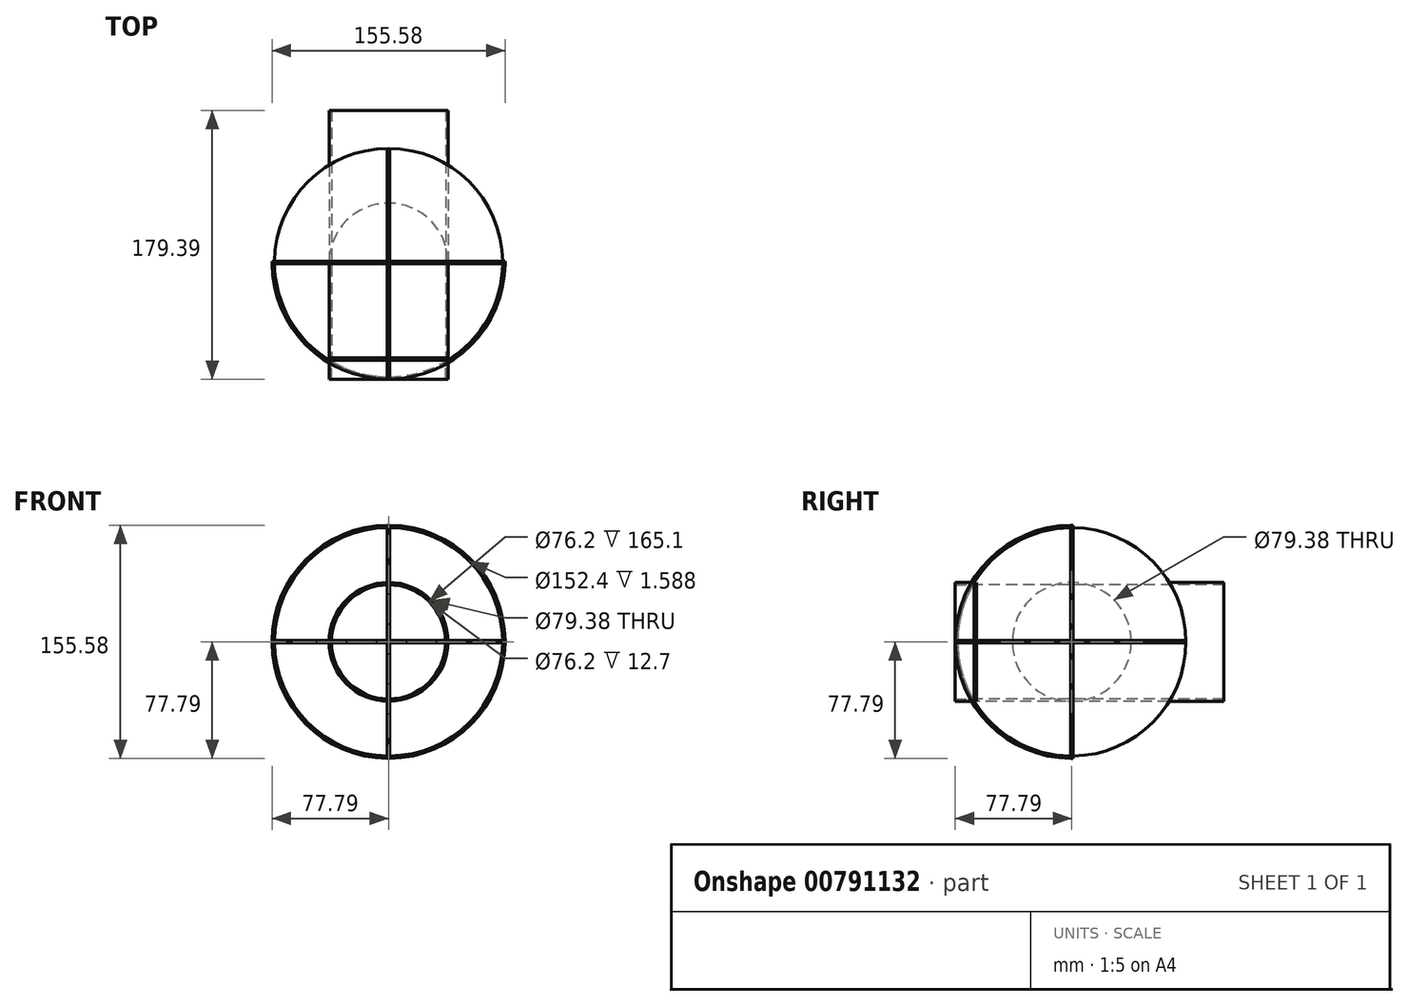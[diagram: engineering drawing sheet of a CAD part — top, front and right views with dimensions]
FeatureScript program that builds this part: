
annotation { "Feature Type Name" : "Feature", "Feature Type Description" : "" }
export const myFeature = defineFeature(function(context is Context, id is Id, definition is map)
    precondition{}
    {
        {
            var Q0;
            Q0=qCreatedBy(makeId("Right.planeOp"),FACE);
            var sketch = newSketch(context, id + "F0", { "sketchPlane" : qUnion([Q0])});
            skCircle(sketch, "E0", {"center": v(0, 0) * mm, "radius": 76.2 * mm});
            skCircle(sketch, "E1", {"center": v(0, 0) * mm, "radius": 38.1 * mm});
            skCircle(sketch, "E2.0", {"center": v(0, 0) * mm, "radius": 39.69 * mm});
            skCircle(sketch, "E3.0", {"center": v(0, 0) * mm, "radius": 77.79 * mm});
            skLineSegment(sketch, "E4", {"start": v(0, 77.79) * mm, "end": v(0, 38.1) * mm});
            skLineSegment(sketch, "E5", {"start": v(0, -38.1) * mm, "end": v(0, -77.79) * mm});
            skSolve(sketch);
        }
        {
            var Q0;
            Q0=qCreatedBy(makeId("Top.planeOp"),FACE);
            var sketch = newSketch(context, id + "F1", { "sketchPlane" : qUnion([Q0])});
            skCircle(sketch, "E6", {"center": v(0, 0) * mm, "radius": 76.2 * mm});
            skCircle(sketch, "E7", {"center": v(0, 0) * mm, "radius": 38.1 * mm});
            skCircle(sketch, "E8.0", {"center": v(0, 0) * mm, "radius": 39.69 * mm});
            skCircle(sketch, "E9.0", {"center": v(0, 0) * mm, "radius": 77.79 * mm});
            skLineSegment(sketch, "E10", {"start": v(-38.1, 0) * mm, "end": v(-77.79, 0) * mm});
            skLineSegment(sketch, "E11", {"start": v(38.1, 0) * mm, "end": v(77.79, 0) * mm});
            skCircle(sketch, "E12", {"center": v(0, 0) * mm, "radius": 66.68 * mm});
            skSolve(sketch);
        }
        {
            var Q0;
            Q0=qCreatedBy(makeId("Front.planeOp"),FACE);
            var sketch = newSketch(context, id + "F2", { "sketchPlane" : qUnion([Q0])});
            skCircle(sketch, "E13", {"center": v(0, 0) * mm, "radius": 76.2 * mm});
            skCircle(sketch, "E14", {"center": v(0, 0) * mm, "radius": 38.1 * mm});
            skCircle(sketch, "E15.0", {"center": v(0, 0) * mm, "radius": 39.69 * mm});
            skCircle(sketch, "E16.0", {"center": v(0, 0) * mm, "radius": 77.79 * mm});
            skSolve(sketch);
        }
        {
            var Q0;
            Q0=makeQuery(id+"F2.imprint","IMPRINT",FACE,{"disambiguationData":[TD([[makeQuery(id+"F2.imprint","IMPRINT",EDGE,{"derivedFrom":sQuery(id+"F2.wireOp",EDGE,"E13")}),-1.0]])]});
            extrude(context, id + "F3", {"entities" : qUnion([Q0]), "endBound" : BoundingType.SYMMETRIC, "oppositeDirection" : true, "depth" : 1.59 * mm, "offsetDistance" : 25.4 * mm});
        }
        {
            var Q0;
            Q0=makeQuery(id+"F2.imprint","IMPRINT",FACE,{"disambiguationData":[TD([[makeQuery(id+"F2.imprint","IMPRINT",EDGE,{"derivedFrom":sQuery(id+"F2.wireOp",EDGE,"E14")}),-1.0]])]});
            extrude(context, id + "F4", {"entities" : qUnion([Q0]), "oppositeDirection" : true, "depth" : 101.6 * mm, "offsetDistance" : 25.4 * mm, "hasSecondDirection" : true, "secondDirectionOppositeDirection" : false, "secondDirectionDepth" : 63.5 * mm});
        }
        {
            var Q0;
            {var subQ0=sQuery(id+"F0.wireOp",EDGE,"E4");var subQ1=sQuery(id+"F0.wireOp",EDGE,"E0");var subQ2=makeQuery(id+"F0.imprint","INTERSECT",VERTEX,{"derivedFrom":[subQ1,subQ0]});Q0=makeQuery(id+"F0.imprint","IMPRINT",FACE,{"disambiguationData":[TD([[makeQuery(id+"F0.imprint","IMPRINT",EDGE,{"disambiguationData":[TD([[subQ2,-1.0]])],"derivedFrom":subQ1}),-1.0]])]});}
            extrude(context, id + "F5", {"entities" : qUnion([Q0]), "endBound" : BoundingType.SYMMETRIC, "depth" : 1.59 * mm, "offsetDistance" : 25.4 * mm});
        }
        {
            var Q0;
            {var subQ0=sQuery(id+"F1.wireOp",EDGE,"E10");var subQ1=sQuery(id+"F1.wireOp",EDGE,"E6");var subQ2=makeQuery(id+"F1.imprint","INTERSECT",VERTEX,{"derivedFrom":[subQ1,subQ0]});Q0=makeQuery(id+"F1.imprint","IMPRINT",FACE,{"disambiguationData":[TD([[makeQuery(id+"F1.imprint","IMPRINT",EDGE,{"disambiguationData":[TD([[subQ2,-1.0]])],"derivedFrom":subQ1}),-1.0]])]});}
            extrude(context, id + "F6", {"entities" : qUnion([Q0]), "operationType" : NewBodyOperationType.ADD, "endBound" : BoundingType.SYMMETRIC, "depth" : 1.59 * mm, "offsetDistance" : 25.4 * mm});
        }
        {
            var Q0;
            Q0=makeQuery(id+"F2.imprint","IMPRINT",FACE,{"disambiguationData":[TD([[makeQuery(id+"F2.imprint","IMPRINT",EDGE,{"derivedFrom":sQuery(id+"F2.wireOp",EDGE,"E14")}),-1.0]])]});
            extrude(context, id + "F7", {"entities" : qUnion([Q0]), "depth" : 77.8 * mm, "offsetDistance" : 25.4 * mm, "hasSecondDirection" : true, "secondDirectionOppositeDirection" : false, "secondDirectionDepth" : 65.1 * mm});
        }
        {
            var Q0;
            {var subQ0=sQuery(id+"F0.wireOp",EDGE,"E4");var subQ1=sQuery(id+"F0.wireOp",EDGE,"E0");var subQ2=makeQuery(id+"F0.imprint","INTERSECT",VERTEX,{"derivedFrom":[subQ1,subQ0]});Q0=makeQuery(id+"F0.imprint","IMPRINT",FACE,{"disambiguationData":[TD([[makeQuery(id+"F0.imprint","IMPRINT",EDGE,{"disambiguationData":[TD([[subQ2,1.0]])],"derivedFrom":subQ1}),1.0]])]});}
            var Q1;
            {var subQ0=sQuery(id+"F0.wireOp",EDGE,"E4");var subQ1=sQuery(id+"F0.wireOp",EDGE,"E0");var subQ2=makeQuery(id+"F0.imprint","INTERSECT",VERTEX,{"derivedFrom":[subQ1,subQ0]});Q1=makeQuery(id+"F0.imprint","IMPRINT",FACE,{"disambiguationData":[TD([[makeQuery(id+"F0.imprint","IMPRINT",EDGE,{"disambiguationData":[TD([[subQ2,-1.0]])],"derivedFrom":subQ1}),1.0]])]});}
            extrude(context, id + "F8", {"entities" : qUnion([Q0, Q1]), "endBound" : BoundingType.SYMMETRIC, "depth" : 1.59 * mm, "offsetDistance" : 25.4 * mm});
        }
        {
            var Q0;
            {var subQ0=sQuery(id+"F1.wireOp",EDGE,"E10");var subQ1=sQuery(id+"F1.wireOp",EDGE,"E8.0");var subQ2=makeQuery(id+"F1.imprint","INTERSECT",VERTEX,{"derivedFrom":[subQ1,subQ0]});Q0=makeQuery(id+"F1.imprint","IMPRINT",FACE,{"disambiguationData":[TD([[makeQuery(id+"F1.imprint","IMPRINT",EDGE,{"disambiguationData":[TD([[subQ2,1.0]])],"derivedFrom":subQ1}),-1.0]])]});}
            var Q1;
            {var subQ0=sQuery(id+"F1.wireOp",EDGE,"E10");var subQ1=sQuery(id+"F1.wireOp",EDGE,"E6");var subQ2=makeQuery(id+"F1.imprint","INTERSECT",VERTEX,{"derivedFrom":[subQ1,subQ0]});Q1=makeQuery(id+"F1.imprint","IMPRINT",FACE,{"disambiguationData":[TD([[makeQuery(id+"F1.imprint","IMPRINT",EDGE,{"disambiguationData":[TD([[subQ2,1.0]])],"derivedFrom":subQ1}),1.0]])]});}
            extrude(context, id + "F9", {"entities" : qUnion([Q0, Q1]), "endBound" : BoundingType.SYMMETRIC, "depth" : 1.59 * mm, "offsetDistance" : 25.4 * mm});
        }
        {
            var Q0;
            Q0=makeQuery(id+"F2.imprint","IMPRINT",FACE,{"disambiguationData":[TD([[makeQuery(id+"F2.imprint","IMPRINT",EDGE,{"derivedFrom":sQuery(id+"F2.wireOp",EDGE,"E13")}),1.0]])]});
            extrude(context, id + "F10", {"entities" : qUnion([Q0]), "endBound" : BoundingType.SYMMETRIC, "depth" : 1.59 * mm, "offsetDistance" : 25.4 * mm});
        }
    });
